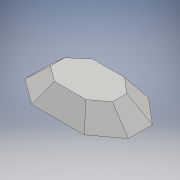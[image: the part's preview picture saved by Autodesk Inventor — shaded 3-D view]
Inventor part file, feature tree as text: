
AUTODESK INVENTOR PART (.ipt)
format: ipt  version: 2016 (Build 200138000, 138)  size: 121,856 bytes
history: native  units: mm
features: sketch x2, plane x1, loft x1, shell x1
ambient origin geometry x8: Origin, YZ Plane, XZ Plane, XY Plane, X Axis, Y Axis, Z Axis, Center Point
bodies: Solid1 (feature_tree)
feature tree (5):
  sketch  "Sketch2"  dims[d19=673.0mm d20=275.5mm d21=251.0mm]
  plane  "Work Plane1"
  loft  "Loft1"
  shell  "Shell1"  Thickness=251.0mm
  sketch  "Sketch3"  dims[d22=349.0mm d23=331.0mm d24=275.5mm d25=534.0mm d26=200.0mm d34=165.3mm d35=150.6mm d36=209.4mm d37=198.6mm d38=165.3mm d39=0.0mm d40=90.0deg d41=0.0mm d42=90.0deg d43=3.0mm]
